AUTODESK INVENTOR PART (.ipt)
format: ipt  version: 2014 (Build 180170000, 170)  size: 99,328 bytes
history: native  units: mm (DEFAULTED — no unit token found)
features: other x3, fillet x2, pattern_linear x1
ambient origin geometry x8: Origin, YZ Plane, XZ Plane, XY Plane, X Axis, Y Axis, Z Axis, Center Point
bodies: Solid1 (feature_tree), Body (feature_tree)
feature tree (6):
  other  "Main Sketch"
  other  "Belt Plane"
  other  "Groove"
  fillet  "Fillet External"  Radius=10.6172mm
  fillet  "Fillet Internal"  Radius=5.934119mm
  pattern_linear  "Groove Pattern"  Spacing1=3.175mm  [1 undecoded]
note: 1 required parameter value undecoded (feature->parameter linkage not recoverable at this tier; creation-order binding heuristic only, values carry confidence <= 0.55)
